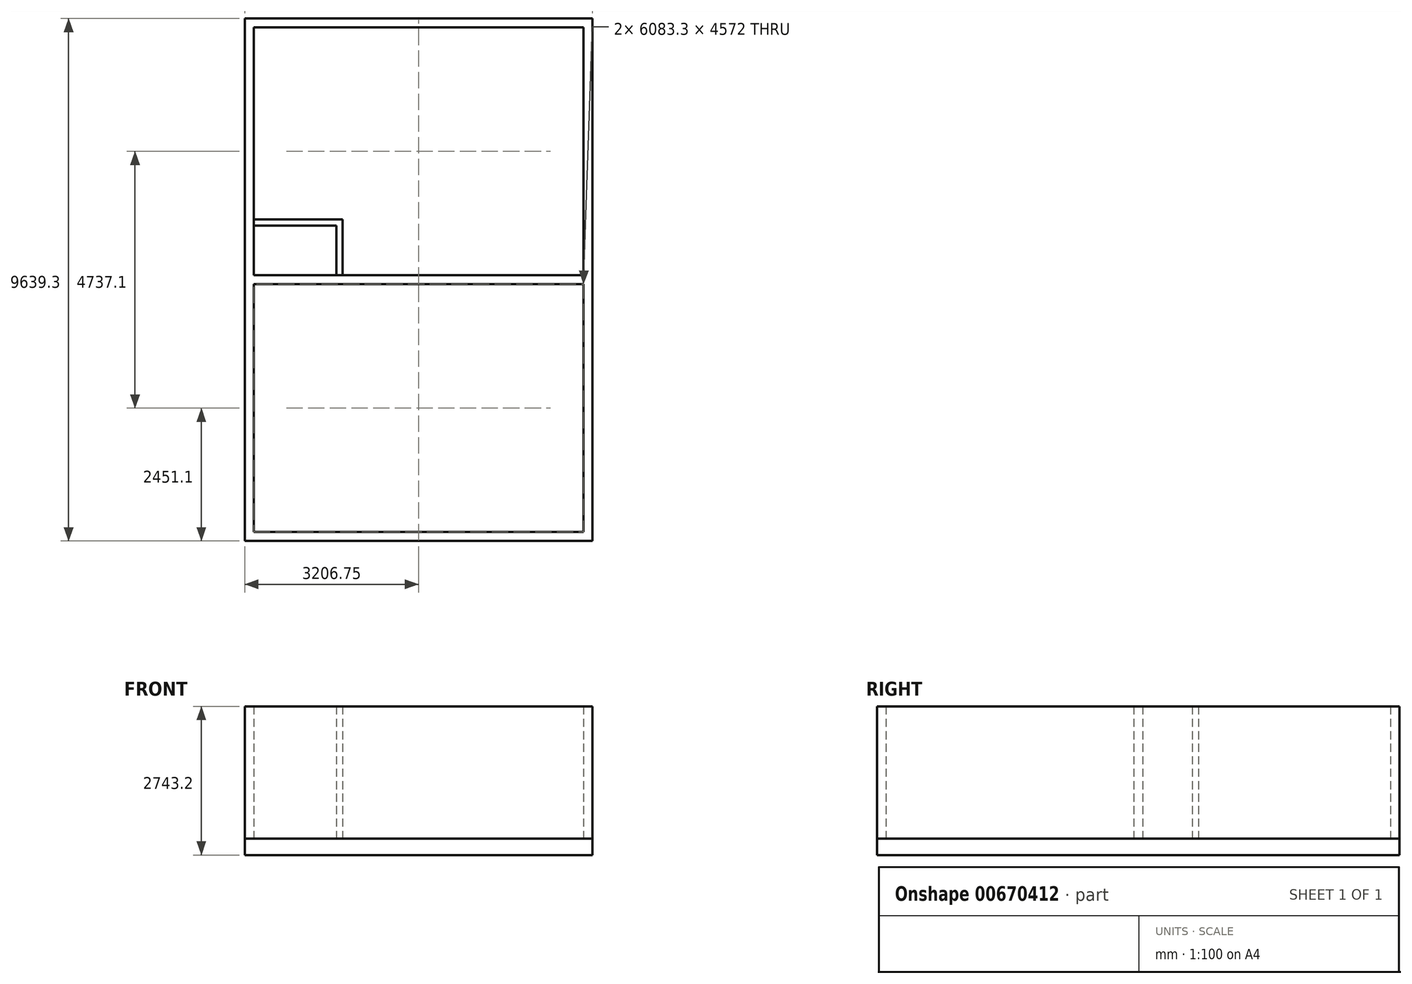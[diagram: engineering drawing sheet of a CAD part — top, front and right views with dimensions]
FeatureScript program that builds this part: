
annotation { "Feature Type Name" : "Feature", "Feature Type Description" : "" }
export const myFeature = defineFeature(function(context is Context, id is Id, definition is map)
    precondition{}
    {
        {
            var Q0;
            Q0=qCreatedBy(makeId("Top.planeOp"),FACE);
            var sketch = newSketch(context, id + "F0", { "sketchPlane" : qUnion([Q0])});
            skLineSegment(sketch, "E0.bottom", {"start": v(-3206.75, 4819.65) * mm, "end": v(3206.75, 4819.65) * mm});
            skLineSegment(sketch, "E0.top", {"start": v(-3206.75, -4819.65) * mm, "end": v(3206.75, -4819.65) * mm});
            skLineSegment(sketch, "E0.left", {"start": v(-3206.75, 4819.65) * mm, "end": v(-3206.75, -4819.65) * mm});
            skLineSegment(sketch, "E0.right", {"start": v(3206.75, 4819.65) * mm, "end": v(3206.75, -4819.65) * mm});
            skPoint(sketch, "E0.middle", {"position": v(0, 0) * mm});
            skLineSegment(sketch, "E1.0", {"start": v(-3041.65, 4654.55) * mm, "end": v(-3041.65, 82.55) * mm});
            skLineSegment(sketch, "E1.1", {"start": v(-3041.65, 4654.55) * mm, "end": v(3041.65, 4654.55) * mm});
            skLineSegment(sketch, "E1.2", {"start": v(3041.65, 4654.55) * mm, "end": v(3041.65, 82.55) * mm});
            skLineSegment(sketch, "E1.3", {"start": v(-3041.65, -4654.55) * mm, "end": v(3041.65, -4654.55) * mm});
            skLineSegment(sketch, "E2.0", {"start": v(-3041.65, 82.55) * mm, "end": v(3041.65, 82.55) * mm});
            skLineSegment(sketch, "E3.trimOffspring", {"start": v(-3041.65, -82.55) * mm, "end": v(-3041.65, -4654.55) * mm});
            skLineSegment(sketch, "E4.trimOffspring", {"start": v(3041.65, -82.55) * mm, "end": v(3041.65, -4654.55) * mm});
            skLineSegment(sketch, "E5", {"start": v(-3041.65, -82.55) * mm, "end": v(3041.65, -82.55) * mm});
            skLineSegment(sketch, "E6", {"start": v(-3041.65, 996.95) * mm, "end": v(-1517.65, 996.95) * mm});
            skLineSegment(sketch, "E7", {"start": v(-1517.65, 996.95) * mm, "end": v(-1517.65, 82.55) * mm});
            skLineSegment(sketch, "E8.0", {"start": v(-1403.35, 1111.25) * mm, "end": v(-1403.35, 82.55) * mm});
            skLineSegment(sketch, "E8.1", {"start": v(-3041.65, 1111.25) * mm, "end": v(-1403.35, 1111.25) * mm});
            skLineSegment(sketch, "E9", {"start": v(-1403.35, 692.15) * mm, "end": v(-793.75, 692.15) * mm});
            skLineSegment(sketch, "E10", {"start": v(-31.75, 692.15) * mm, "end": v(-31.75, 82.55) * mm});
            skLineSegment(sketch, "E11", {"start": v(-793.75, 692.15) * mm, "end": v(-793.75, 82.55) * mm});
            skLineSegment(sketch, "E12", {"start": v(-641.35, 692.15) * mm, "end": v(-641.35, 82.55) * mm});
            skLineSegment(sketch, "E13.trimOffspring", {"start": v(-641.35, 692.15) * mm, "end": v(-31.75, 692.15) * mm});
            skCircle(sketch, "E14", {"center": v(2279.65, 844.55) * mm, "radius": 609.6 * mm});
            skCircle(sketch, "E15", {"center": v(2279.65, 844.55) * mm, "radius": 76.2 * mm});
            skPoint(sketch, "E16", {"position": v(2279.65, 1454.15) * mm});
            skLineSegment(sketch, "E17", {"start": v(2279.65, 844.55) * mm, "end": v(2279.65, 1454.15) * mm});
            skLineSegment(sketch, "E18", {"start": v(2279.65, 844.55) * mm, "end": v(1670.05, 844.55) * mm});
            skLineSegment(sketch, "E19", {"start": v(2279.65, 844.55) * mm, "end": v(2279.65, 234.95) * mm});
            skLineSegment(sketch, "E20", {"start": v(2279.65, 844.55) * mm, "end": v(2889.25, 844.55) * mm});
            skLineSegment(sketch, "E21", {"start": v(2279.65, 844.55) * mm, "end": v(1751.72, 1149.35) * mm});
            skLineSegment(sketch, "E22", {"start": v(2279.65, 844.55) * mm, "end": v(1974.85, 1372.48) * mm});
            skLineSegment(sketch, "E23", {"start": v(2279.65, 844.55) * mm, "end": v(1751.72, 539.75) * mm});
            skLineSegment(sketch, "E24", {"start": v(2279.65, 844.55) * mm, "end": v(1974.85, 316.62) * mm});
            skLineSegment(sketch, "E25", {"start": v(2279.65, 844.55) * mm, "end": v(2584.45, 316.62) * mm});
            skLineSegment(sketch, "E26", {"start": v(2279.65, 844.55) * mm, "end": v(2807.58, 539.75) * mm});
            skLineSegment(sketch, "E27", {"start": v(2279.65, 844.55) * mm, "end": v(2807.58, 1149.35) * mm});
            skLineSegment(sketch, "E28", {"start": v(2279.65, 844.55) * mm, "end": v(2584.45, 1372.48) * mm});
            skSolve(sketch);
        }
        {
            var Q0;
            Q0 = qSketchRegion(id + "F0", true);
            var Q1;
            Q1=makeQuery(id+"F0.imprint","IMPRINT",FACE,{"disambiguationData":[TD([[makeQuery(id+"F0.imprint","IMPRINT",EDGE,{"derivedFrom":sQuery(id+"F0.wireOp",EDGE,"E1.3")}),1.0]])]});
            var Q2;
            Q2=makeQuery(id+"F0.imprint","IMPRINT",FACE,{"disambiguationData":[TD([[makeQuery(id+"F0.imprint","IMPRINT",EDGE,{"derivedFrom":sQuery(id+"F0.wireOp",EDGE,"E14")}),1.0]])]});
            var Q3;
            Q3=makeQuery(id+"F0.imprint","IMPRINT",FACE,{"disambiguationData":[TD([[makeQuery(id+"F0.imprint","IMPRINT",EDGE,{"derivedFrom":sQuery(id+"F0.wireOp",EDGE,"E15")}),1.0]])]});
            var Q4;
            {var subQ7=sQuery(id+"F0.wireOp",EDGE,"E1.1");Q4=makeQuery(id+"F0.imprint","IMPRINT",FACE,{"disambiguationData":[TD([[makeQuery(id+"F0.imprint","IMPRINT",EDGE,{"derivedFrom":subQ7}),-1.0]])]});}
            var Q5;
            {var subQ0=sQuery(id+"F0.wireOp",EDGE,"E10");Q5=makeQuery(id+"F0.imprint","IMPRINT",FACE,{"disambiguationData":[TD([[makeQuery(id+"F0.imprint","IMPRINT",EDGE,{"derivedFrom":subQ0}),-1.0]])]});}
            var Q6;
            {var subQ4=sQuery(id+"F0.wireOp",EDGE,"E9");Q6=makeQuery(id+"F0.imprint","IMPRINT",FACE,{"disambiguationData":[TD([[makeQuery(id+"F0.imprint","IMPRINT",EDGE,{"derivedFrom":subQ4}),-1.0]])]});}
            var Q7;
            {var subQ0=sQuery(id+"F0.wireOp",EDGE,"E6");Q7=makeQuery(id+"F0.imprint","IMPRINT",FACE,{"disambiguationData":[TD([[makeQuery(id+"F0.imprint","IMPRINT",EDGE,{"derivedFrom":subQ0}),1.0]])]});}
            var Q8;
            {var subQ3=sQuery(id+"F0.wireOp",EDGE,"E6");Q8=makeQuery(id+"F0.imprint","IMPRINT",FACE,{"disambiguationData":[TD([[makeQuery(id+"F0.imprint","IMPRINT",EDGE,{"derivedFrom":subQ3}),-1.0]])]});}
            extrude(context, id + "F1", {"entities" : qUnion([Q0, Q1, Q2, Q3, Q4, Q5, Q6, Q7, Q8]), "oppositeDirection" : true, "depth" : 304.8 * mm, "offsetDistance" : 25.4 * mm});
        }
        {
            var Q0;
            Q0 = qSketchRegion(id + "F0", true);
            extrude(context, id + "F2", {"entities" : qUnion([Q0]), "depth" : 2438.4 * mm, "offsetDistance" : 25.4 * mm});
        }
        {
            var Q0;
            {var subQ0=sQuery(id+"F0.wireOp",EDGE,"E6");Q0=makeQuery(id+"F0.imprint","IMPRINT",FACE,{"disambiguationData":[TD([[makeQuery(id+"F0.imprint","IMPRINT",EDGE,{"derivedFrom":subQ0}),1.0]])]});}
            extrude(context, id + "F3", {"entities" : qUnion([Q0]), "depth" : 2438.4 * mm, "offsetDistance" : 25.4 * mm});
        }
    });
